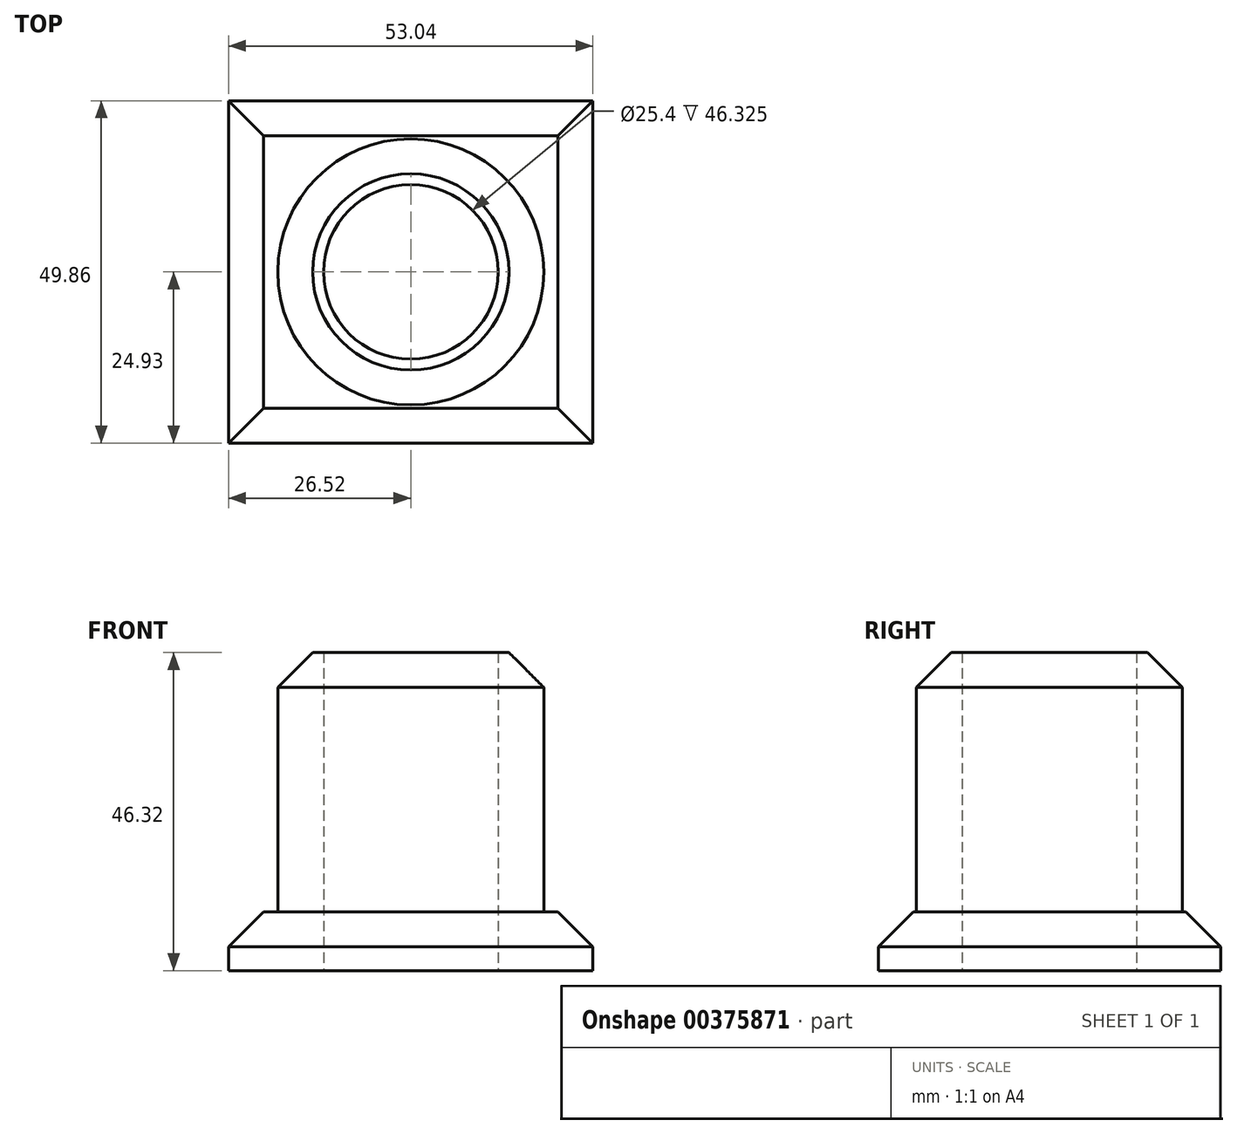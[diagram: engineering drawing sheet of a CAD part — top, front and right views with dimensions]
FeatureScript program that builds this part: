
annotation { "Feature Type Name" : "Feature", "Feature Type Description" : "" }
export const myFeature = defineFeature(function(context is Context, id is Id, definition is map)
    precondition{}
    {
        {
            var Q0;
            Q0=qCreatedBy(makeId("Top.planeOp"),FACE);
            var sketch = newSketch(context, id + "F0", { "sketchPlane" : qUnion([Q0])});
            skCircle(sketch, "E0", {"center": v(0, 0) * mm, "radius": 19.37 * mm});
            skSolve(sketch);
        }
        {
            var Q0;
            Q0=makeQuery(id+"F0.imprint","IMPRINT",FACE,{"disambiguationData":[TD([[makeQuery(id+"F0.imprint","IMPRINT",EDGE,{"derivedFrom":sQuery(id+"F0.wireOp",EDGE,"E0")}),1.0]])]});
            extrude(context, id + "F1", {"entities" : qUnion([Q0]), "depth" : 9.94 * mm});
        }
        {
            var Q0;
            Q0=qCreatedBy(makeId("Top.planeOp"),FACE);
            var sketch = newSketch(context, id + "F2", { "sketchPlane" : qUnion([Q0])});
            skLineSegment(sketch, "E1.bottom", {"start": v(-26.52, 24.93) * mm, "end": v(26.52, 24.93) * mm});
            skLineSegment(sketch, "E1.top", {"start": v(-26.52, -24.93) * mm, "end": v(26.52, -24.93) * mm});
            skLineSegment(sketch, "E1.left", {"start": v(-26.52, 24.93) * mm, "end": v(-26.52, -24.93) * mm});
            skLineSegment(sketch, "E1.right", {"start": v(26.52, 24.93) * mm, "end": v(26.52, -24.93) * mm});
            skPoint(sketch, "E1.middle", {"position": v(0, 0) * mm});
            skSolve(sketch);
        }
        {
            var Q0;
            Q0=makeQuery(id+"F2.imprint","IMPRINT",FACE,{"disambiguationData":[TD([[makeQuery(id+"F2.imprint","IMPRINT",EDGE,{"derivedFrom":sQuery(id+"F2.wireOp",EDGE,"E1.bottom")}),-1.0]])]});
            extrude(context, id + "F3", {"entities" : qUnion([Q0]), "operationType" : NewBodyOperationType.ADD, "oppositeDirection" : true, "depth" : 8.53 * mm});
        }
        {
            var Q0;
            Q0=makeQuery(id+"F3.opExtrude","CAP_FACE",FACE,{"disambiguationData":[OSD([sQuery(id+"F2.wireOp",EDGE,"E1.bottom"),sQuery(id+"F2.wireOp",EDGE,"E1.top"),sQuery(id+"F2.wireOp",EDGE,"E1.left"),sQuery(id+"F2.wireOp",EDGE,"E1.right")])],"isStart":false});
            var sketch = newSketch(context, id + "F4", { "sketchPlane" : qUnion([Q0])});
            skPoint(sketch, "E2", {"position": v(0, 0) * mm});
            skSolve(sketch);
        }
        {
            var Q0;
            Q0=sQuery(id+"F4.wireOp",VERTEX,"E2");
            var Q1;
            Q1=makeQuery(id+"F1.opExtrude","SWEPT_BODY",BODY,{"disambiguationData":[OSD([sQuery(id+"F0.wireOp",EDGE,"E0")])]});
            hole(context, id + "F5", {"style" : HoleStyle.SIMPLE, "endStyle" : HoleEndStyle.THROUGH, "holeDiameter" : 25.4 * mm, "isTappedThrough" : true, "tappedDepth" : 12.7 * mm, "tapClearance" : 3, "locations" : qUnion([Q0]), "scope" : qUnion([Q1])});
        }
        {
            var Q0;
            Q0=makeQuery(id+"F1.opExtrude","CAP_FACE",FACE,{"disambiguationData":[OSD([sQuery(id+"F0.wireOp",EDGE,"E0")])],"isStart":false});
            extrude(context, id + "F6", {"entities" : qUnion([Q0]), "operationType" : NewBodyOperationType.ADD, "depth" : 27.86 * mm});
        }
        {
            var Q0;
            Q0=makeQuery(id+"F6.opExtrude","CAP_EDGE",EDGE,{"disambiguationData":[OSD([sQuery(id+"F0.wireOp",EDGE,"E0")])],"isStart":false});
            chamfer(context, id + "F7", {"entities" : qUnion([Q0]), "width" : 5.08 * mm, "tangentPropagation" : true});
        }
        {
            var Q0;
            Q0=makeQuery(id+"F3.opExtrude","CAP_EDGE",EDGE,{"disambiguationData":[OSD([sQuery(id+"F2.wireOp",EDGE,"E1.right")])],"isStart":true});
            var Q1;
            Q1=makeQuery(id+"F3.opExtrude","CAP_EDGE",EDGE,{"disambiguationData":[OSD([sQuery(id+"F2.wireOp",EDGE,"E1.top")])],"isStart":true});
            var Q2;
            Q2=makeQuery(id+"F3.opExtrude","CAP_EDGE",EDGE,{"disambiguationData":[OSD([sQuery(id+"F2.wireOp",EDGE,"E1.left")])],"isStart":true});
            var Q3;
            Q3=makeQuery(id+"F3.opExtrude","CAP_EDGE",EDGE,{"disambiguationData":[OSD([sQuery(id+"F2.wireOp",EDGE,"E1.bottom")])],"isStart":true});
            chamfer(context, id + "F8", {"entities" : qUnion([Q0, Q1, Q2, Q3]), "width" : 5.08 * mm, "tangentPropagation" : true});
        }
    });
